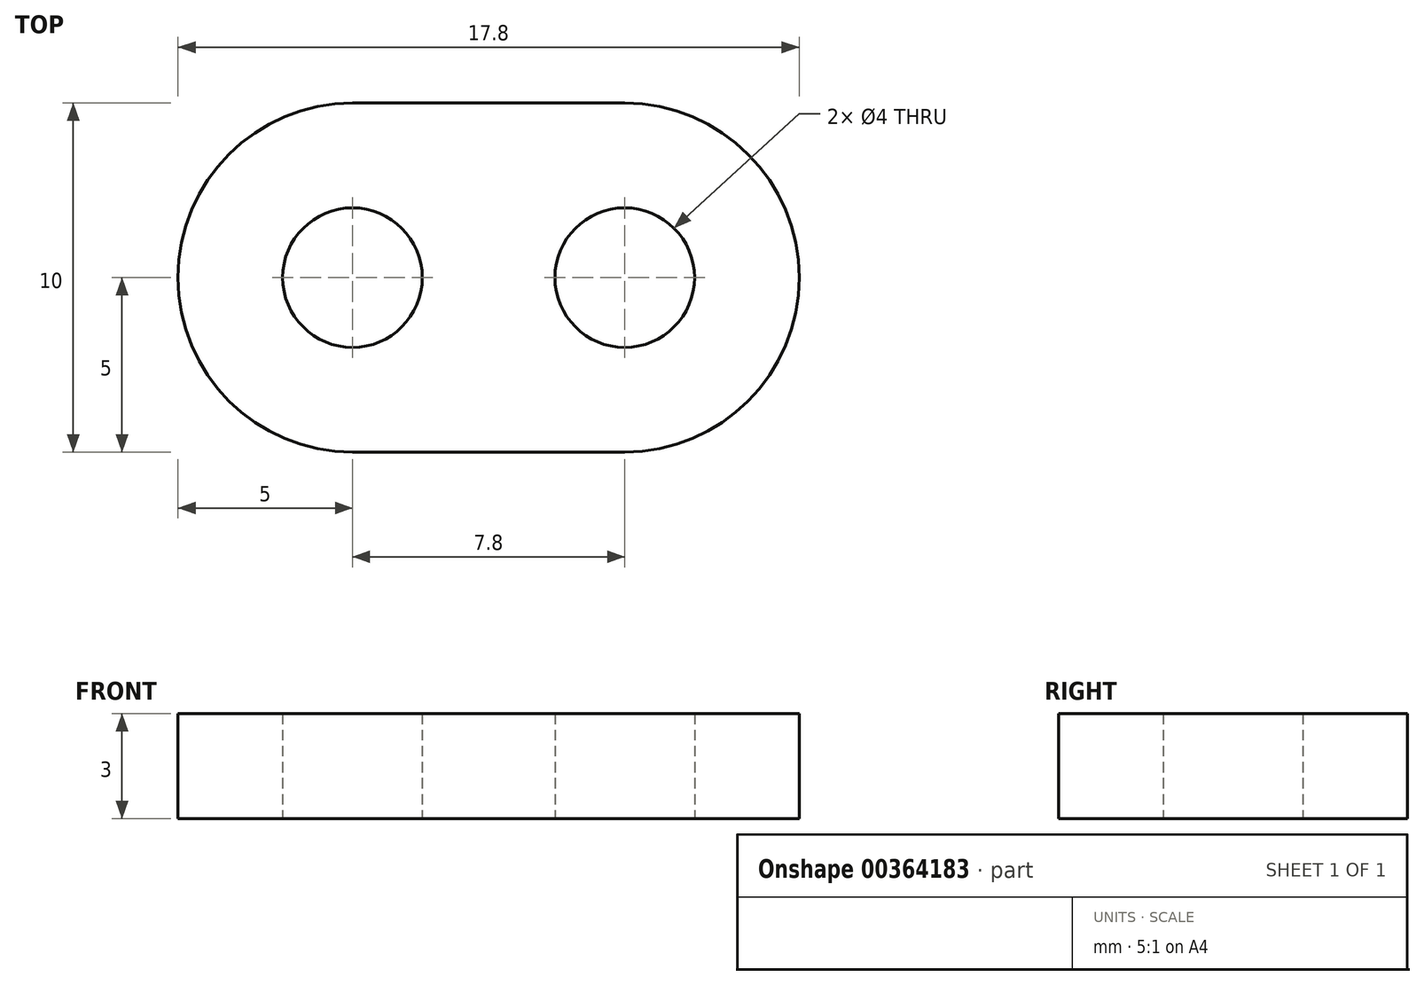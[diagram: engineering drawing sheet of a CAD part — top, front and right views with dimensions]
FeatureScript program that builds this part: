
annotation { "Feature Type Name" : "Feature", "Feature Type Description" : "" }
export const myFeature = defineFeature(function(context is Context, id is Id, definition is map)
    precondition{}
    {
        {
            var Q0;
            Q0=qCreatedBy(makeId("Top.planeOp"),FACE);
            var sketch = newSketch(context, id + "F0", { "sketchPlane" : qUnion([Q0])});
            skLineSegment(sketch, "E0.bottom", {"start": v(3.9, 5) * mm, "end": v(-3.9, 5) * mm});
            skLineSegment(sketch, "E0.top", {"start": v(3.9, -5) * mm, "end": v(-3.9, -5) * mm});
            skPoint(sketch, "E0.middle", {"position": v(0, 0) * mm});
            skCircle(sketch, "E1", {"center": v(-3.9, 0) * mm, "radius": 2 * mm});
            skCircle(sketch, "E2", {"center": v(3.9, 0) * mm, "radius": 2 * mm});
            skArc(sketch, "E3", {"start": v(-3.9, 5) * mm, "mid": v(-8.9, 0) * mm, "end": v(-3.9, -5) * mm});
            skArc(sketch, "E4", {"start": v(3.9, -5) * mm, "mid": v(8.9, 0) * mm, "end": v(3.9, 5) * mm});
            skSolve(sketch);
        }
        {
            var Q0;
            Q0=qSketchRegion(id+"F0",true);
            extrude(context, id + "F1", {"entities" : qUnion([Q0]), "depth" : 3 * mm});
        }
    });
